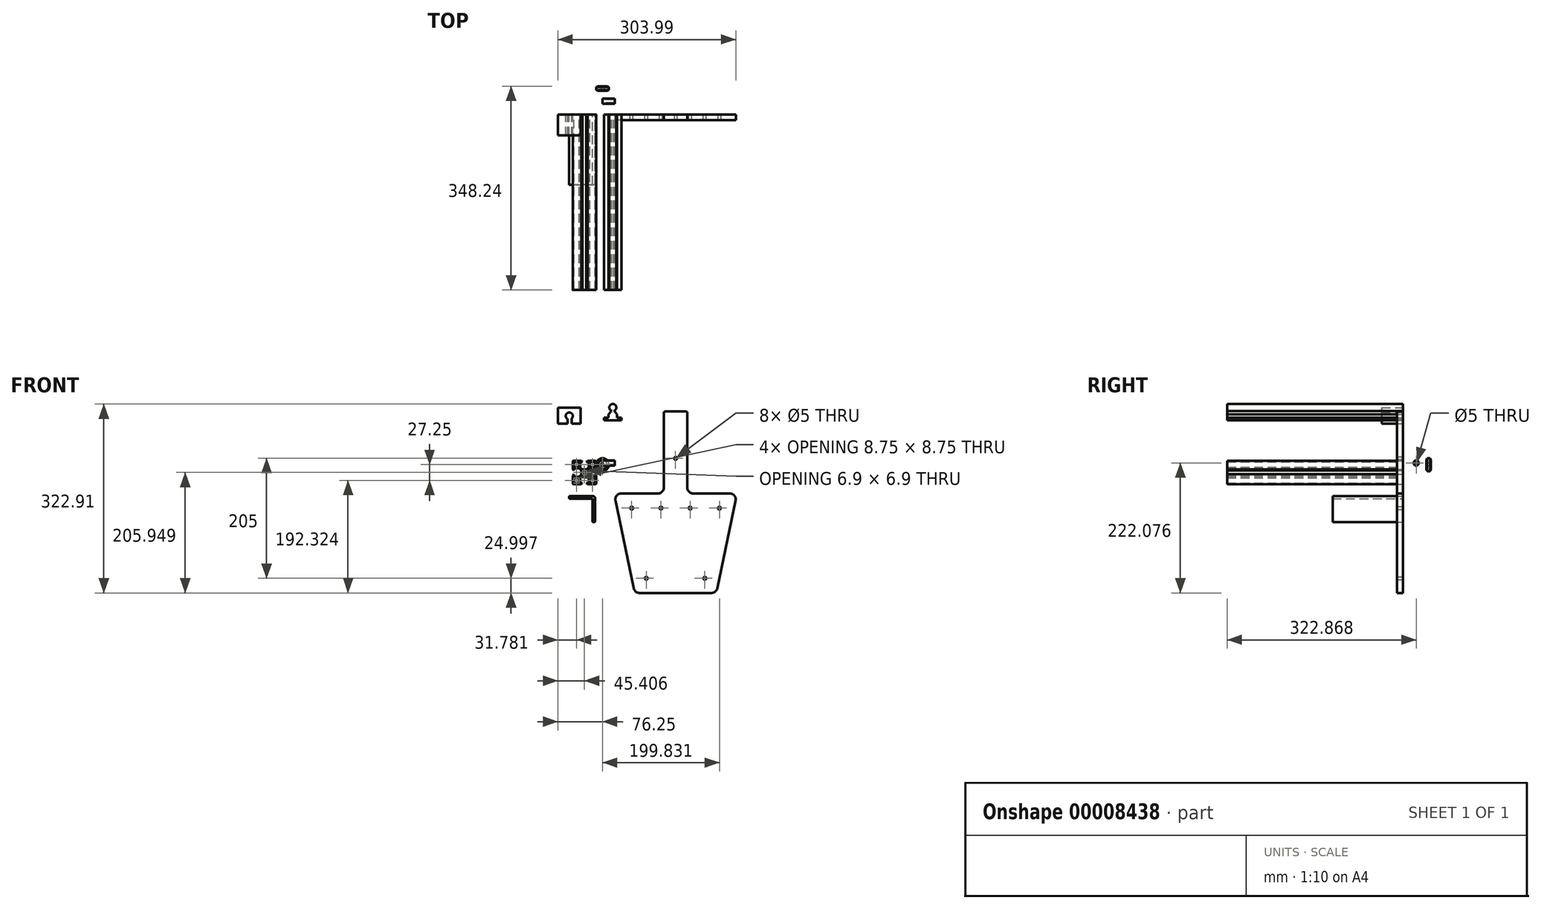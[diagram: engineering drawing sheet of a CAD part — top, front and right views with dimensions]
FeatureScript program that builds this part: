
annotation { "Feature Type Name" : "Feature", "Feature Type Description" : "" }
export const myFeature = defineFeature(function(context is Context, id is Id, definition is map)
    precondition{}
    {
        {
            var Q0;
            Q0=qCreatedBy(makeId("Front.planeOp"),FACE);
            var sketch = newSketch(context, id + "F0", { "sketchPlane" : qUnion([Q0])});
            skLineSegment(sketch, "E0", {"start": v(-49.84, 48.39) * mm, "end": v(-36.1, 48.39) * mm});
            skLineSegment(sketch, "E1", {"start": v(-36.1, 48.39) * mm, "end": v(-34.1, 46.39) * mm});
            skLineSegment(sketch, "E2", {"start": v(-34.1, 46.39) * mm, "end": v(-38.1, 46.39) * mm});
            skLineSegment(sketch, "E3", {"start": v(-48.84, 45.39) * mm, "end": v(-48.84, 38.64) * mm});
            skLineSegment(sketch, "E4", {"start": v(-48.84, 31.64) * mm, "end": v(-50.84, 33.64) * mm});
            skLineSegment(sketch, "E5", {"start": v(-50.84, 33.64) * mm, "end": v(-50.84, 47.39) * mm});
            skLineSegment(sketch, "E6", {"start": v(-50.84, 23.14) * mm, "end": v(-48.84, 25.14) * mm});
            skLineSegment(sketch, "E7", {"start": v(-48.84, 25.14) * mm, "end": v(-48.84, 22.14) * mm});
            skLineSegment(sketch, "E8", {"start": v(-47.84, 10.39) * mm, "end": v(-41.1, 10.39) * mm});
            skLineSegment(sketch, "E9", {"start": v(-34.1, 10.39) * mm, "end": v(-35.8, 8.68) * mm});
            skLineSegment(sketch, "E10", {"start": v(-36.5, 8.39) * mm, "end": v(-49.84, 8.39) * mm});
            skLineSegment(sketch, "E11", {"start": v(-50.84, 9.39) * mm, "end": v(-50.84, 23.14) * mm});
            skLineSegment(sketch, "E12", {"start": v(-25.6, 48.39) * mm, "end": v(-11.84, 48.39) * mm});
            skLineSegment(sketch, "E13", {"start": v(-10.84, 47.39) * mm, "end": v(-10.84, 33.64) * mm});
            skLineSegment(sketch, "E14", {"start": v(-10.84, 33.64) * mm, "end": v(-12.84, 31.64) * mm});
            skLineSegment(sketch, "E15", {"start": v(-12.84, 31.64) * mm, "end": v(-12.84, 34.64) * mm});
            skLineSegment(sketch, "E16", {"start": v(-13.84, 46.39) * mm, "end": v(-20.6, 46.39) * mm});
            skLineSegment(sketch, "E17", {"start": v(-27.6, 46.39) * mm, "end": v(-25.6, 48.39) * mm});
            skLineSegment(sketch, "E18", {"start": v(-10.84, 9.39) * mm, "end": v(-10.84, 22.72) * mm});
            skLineSegment(sketch, "E19", {"start": v(-11.14, 23.43) * mm, "end": v(-12.84, 25.14) * mm});
            skLineSegment(sketch, "E20", {"start": v(-12.84, 25.14) * mm, "end": v(-12.84, 22.14) * mm});
            skLineSegment(sketch, "E21", {"start": v(-13.84, 10.39) * mm, "end": v(-20.6, 10.39) * mm});
            skLineSegment(sketch, "E22", {"start": v(-27.6, 10.39) * mm, "end": v(-25.89, 8.68) * mm});
            skLineSegment(sketch, "E23", {"start": v(-25.18, 8.39) * mm, "end": v(-11.84, 8.39) * mm});
            skLineSegment(sketch, "E24", {"start": v(-48.84, 10.39) * mm, "end": v(-12.84, 46.39) * mm, "construction": true});
            skLineSegment(sketch, "E25", {"start": v(-48.84, 46.39) * mm, "end": v(-12.84, 10.39) * mm, "construction": true});
            skLineSegment(sketch, "E26", {"start": v(-40.1, 45.39) * mm, "end": v(-40.1, 38.64) * mm});
            skLineSegment(sketch, "E27", {"start": v(-41.1, 37.64) * mm, "end": v(-47.84, 37.64) * mm});
            skLineSegment(sketch, "E28", {"start": v(-13.84, 37.64) * mm, "end": v(-20.6, 37.64) * mm});
            skLineSegment(sketch, "E29", {"start": v(-21.6, 38.64) * mm, "end": v(-21.6, 45.39) * mm});
            skLineSegment(sketch, "E30", {"start": v(-47.84, 35.64) * mm, "end": v(-39.92, 35.64) * mm});
            skLineSegment(sketch, "E31", {"start": v(-38.1, 37.1) * mm, "end": v(-38.1, 46.39) * mm});
            skLineSegment(sketch, "E32", {"start": v(-23.6, 45.39) * mm, "end": v(-23.6, 37.47) * mm});
            skLineSegment(sketch, "E33", {"start": v(-21.77, 35.64) * mm, "end": v(-13.84, 35.64) * mm});
            skLineSegment(sketch, "E34.bottom", {"start": v(-34.74, 33.84) * mm, "end": v(-27.22, 33.84) * mm});
            skLineSegment(sketch, "E34.top", {"start": v(-34.46, 22.94) * mm, "end": v(-27.22, 22.94) * mm});
            skLineSegment(sketch, "E34.left", {"start": v(-36.3, 32) * mm, "end": v(-36.3, 24.77) * mm});
            skLineSegment(sketch, "E34.right", {"start": v(-25.4, 32) * mm, "end": v(-25.4, 24.77) * mm});
            skLineSegment(sketch, "E35.bottom", {"start": v(-33.3, 31.84) * mm, "end": v(-28.4, 31.84) * mm});
            skLineSegment(sketch, "E35.top", {"start": v(-33.3, 24.94) * mm, "end": v(-28.4, 24.94) * mm});
            skLineSegment(sketch, "E35.left", {"start": v(-34.3, 30.84) * mm, "end": v(-34.3, 25.94) * mm});
            skLineSegment(sketch, "E35.right", {"start": v(-27.4, 30.84) * mm, "end": v(-27.4, 25.94) * mm});
            skLineSegment(sketch, "E36", {"start": v(-23.89, 36.76) * mm, "end": v(-26.52, 34.13) * mm});
            skLineSegment(sketch, "E37", {"start": v(-25.1, 32.72) * mm, "end": v(-22.47, 35.35) * mm});
            skLineSegment(sketch, "E38", {"start": v(-35.44, 34.12) * mm, "end": v(-37.79, 36.39) * mm});
            skLineSegment(sketch, "E39", {"start": v(-47.84, 19.14) * mm, "end": v(-41.1, 19.14) * mm});
            skLineSegment(sketch, "E40", {"start": v(-40.1, 18.14) * mm, "end": v(-40.1, 11.39) * mm});
            skLineSegment(sketch, "E41", {"start": v(-47.84, 21.14) * mm, "end": v(-39.92, 21.14) * mm});
            skLineSegment(sketch, "E42", {"start": v(-38.1, 19.31) * mm, "end": v(-38.1, 11.39) * mm});
            skLineSegment(sketch, "E43", {"start": v(-21.6, 11.39) * mm, "end": v(-21.6, 18.14) * mm});
            skLineSegment(sketch, "E44", {"start": v(-20.6, 19.14) * mm, "end": v(-13.84, 19.14) * mm});
            skLineSegment(sketch, "E45", {"start": v(-21.77, 21.14) * mm, "end": v(-13.84, 21.14) * mm});
            skLineSegment(sketch, "E46", {"start": v(-23.6, 19.31) * mm, "end": v(-23.6, 11.39) * mm});
            skLineSegment(sketch, "E47", {"start": v(-35.17, 22.65) * mm, "end": v(-37.8, 20.02) * mm});
            skLineSegment(sketch, "E48", {"start": v(-39.22, 21.43) * mm, "end": v(-36.59, 24.06) * mm});
            skLineSegment(sketch, "E49", {"start": v(-22.47, 21.43) * mm, "end": v(-25.1, 24.06) * mm});
            skLineSegment(sketch, "E50", {"start": v(-36.59, 32.72) * mm, "end": v(-39.22, 35.35) * mm});
            skLineSegment(sketch, "E51", {"start": v(-23.89, 20.02) * mm, "end": v(-26.52, 22.65) * mm});
            skLineSegment(sketch, "E52.trimOffspring", {"start": v(-41.1, 46.39) * mm, "end": v(-47.84, 46.39) * mm});
            skLineSegment(sketch, "E53.trimOffspring", {"start": v(-48.84, 34.64) * mm, "end": v(-48.84, 31.64) * mm});
            skLineSegment(sketch, "E54.trimOffspring", {"start": v(-24.6, 46.39) * mm, "end": v(-27.6, 46.39) * mm});
            skLineSegment(sketch, "E55.trimOffspring", {"start": v(-12.84, 38.64) * mm, "end": v(-12.84, 45.39) * mm});
            skPoint(sketch, "E56.orphan", {"position": v(-23.6, 35.64) * mm});
            skLineSegment(sketch, "E57.trimOffspring", {"start": v(-12.84, 18.14) * mm, "end": v(-12.84, 11.39) * mm});
            skLineSegment(sketch, "E58.trimOffspring", {"start": v(-24.6, 10.39) * mm, "end": v(-27.6, 10.39) * mm});
            skLineSegment(sketch, "E59.trimOffspring", {"start": v(-37.1, 10.39) * mm, "end": v(-34.1, 10.39) * mm});
            skPoint(sketch, "E60.orphan", {"position": v(-38.1, 21.14) * mm});
            skLineSegment(sketch, "E61.trimOffspring", {"start": v(-48.84, 18.14) * mm, "end": v(-48.84, 11.39) * mm});
            skPoint(sketch, "E62.visualSharp", {"position": v(-48.84, 21.14) * mm});
            skArc(sketch, "E62.filletArc", {"start": v(-48.84, 22.14) * mm, "mid": v(-48.55, 21.43) * mm, "end": v(-47.84, 21.14) * mm});
            skPoint(sketch, "E63.visualSharp", {"position": v(-48.84, 19.14) * mm});
            skArc(sketch, "E63.filletArc", {"start": v(-47.84, 19.14) * mm, "mid": v(-48.55, 18.85) * mm, "end": v(-48.84, 18.14) * mm});
            skPoint(sketch, "E64.visualSharp", {"position": v(-40.1, 19.14) * mm});
            skArc(sketch, "E64.filletArc", {"start": v(-40.1, 18.14) * mm, "mid": v(-40.39, 18.85) * mm, "end": v(-41.1, 19.14) * mm});
            skPoint(sketch, "E65.visualSharp", {"position": v(-40.1, 10.39) * mm});
            skArc(sketch, "E65.filletArc", {"start": v(-41.1, 10.39) * mm, "mid": v(-40.39, 10.68) * mm, "end": v(-40.1, 11.39) * mm});
            skPoint(sketch, "E66.visualSharp", {"position": v(-48.84, 10.39) * mm});
            skArc(sketch, "E66.filletArc", {"start": v(-48.84, 11.39) * mm, "mid": v(-48.55, 10.68) * mm, "end": v(-47.84, 10.39) * mm});
            skPoint(sketch, "E67.visualSharp", {"position": v(-50.84, 8.39) * mm});
            skArc(sketch, "E67.filletArc", {"start": v(-50.84, 9.39) * mm, "mid": v(-50.55, 8.68) * mm, "end": v(-49.84, 8.39) * mm});
            skPoint(sketch, "E68.visualSharp", {"position": v(-36.1, 8.39) * mm});
            skArc(sketch, "E68.filletArc", {"start": v(-36.5, 8.39) * mm, "mid": v(-36.13, 8.46) * mm, "end": v(-35.8, 8.68) * mm});
            skPoint(sketch, "E69.visualSharp", {"position": v(-38.1, 10.39) * mm});
            skArc(sketch, "E69.filletArc", {"start": v(-38.1, 11.39) * mm, "mid": v(-37.8, 10.68) * mm, "end": v(-37.1, 10.39) * mm});
            skPoint(sketch, "E70.visualSharp", {"position": v(-38.1, 19.72) * mm});
            skArc(sketch, "E70.filletArc", {"start": v(-37.8, 20.02) * mm, "mid": v(-38.02, 19.7) * mm, "end": v(-38.1, 19.31) * mm});
            skPoint(sketch, "E71.visualSharp", {"position": v(-39.5, 21.14) * mm});
            skArc(sketch, "E71.filletArc", {"start": v(-39.92, 21.14) * mm, "mid": v(-39.54, 21.21) * mm, "end": v(-39.22, 21.43) * mm});
            skPoint(sketch, "E72.visualSharp", {"position": v(-34.88, 22.94) * mm});
            skArc(sketch, "E72.filletArc", {"start": v(-34.46, 22.94) * mm, "mid": v(-34.85, 22.86) * mm, "end": v(-35.17, 22.65) * mm});
            skPoint(sketch, "E73.visualSharp", {"position": v(-36.3, 24.35) * mm});
            skArc(sketch, "E73.filletArc", {"start": v(-36.59, 24.06) * mm, "mid": v(-36.37, 24.39) * mm, "end": v(-36.3, 24.77) * mm});
            skPoint(sketch, "E74.visualSharp", {"position": v(-10.84, 8.39) * mm});
            skArc(sketch, "E74.filletArc", {"start": v(-11.84, 8.39) * mm, "mid": v(-11.14, 8.68) * mm, "end": v(-10.84, 9.39) * mm});
            skPoint(sketch, "E75.visualSharp", {"position": v(-12.84, 10.39) * mm});
            skArc(sketch, "E75.filletArc", {"start": v(-13.84, 10.39) * mm, "mid": v(-13.14, 10.68) * mm, "end": v(-12.84, 11.39) * mm});
            skPoint(sketch, "E76.visualSharp", {"position": v(-21.6, 10.39) * mm});
            skArc(sketch, "E76.filletArc", {"start": v(-21.6, 11.39) * mm, "mid": v(-21.3, 10.68) * mm, "end": v(-20.6, 10.39) * mm});
            skPoint(sketch, "E77.visualSharp", {"position": v(-23.6, 10.39) * mm});
            skArc(sketch, "E77.filletArc", {"start": v(-24.6, 10.39) * mm, "mid": v(-23.89, 10.68) * mm, "end": v(-23.6, 11.39) * mm});
            skPoint(sketch, "E78.visualSharp", {"position": v(-25.6, 8.39) * mm});
            skArc(sketch, "E78.filletArc", {"start": v(-25.89, 8.68) * mm, "mid": v(-25.56, 8.46) * mm, "end": v(-25.18, 8.39) * mm});
            skPoint(sketch, "E79.visualSharp", {"position": v(-12.84, 19.14) * mm});
            skArc(sketch, "E79.filletArc", {"start": v(-12.84, 18.14) * mm, "mid": v(-13.14, 18.85) * mm, "end": v(-13.84, 19.14) * mm});
            skPoint(sketch, "E80.visualSharp", {"position": v(-21.6, 19.14) * mm});
            skArc(sketch, "E80.filletArc", {"start": v(-20.6, 19.14) * mm, "mid": v(-21.3, 18.85) * mm, "end": v(-21.6, 18.14) * mm});
            skPoint(sketch, "E81.orphan", {"position": v(-23.6, 21.14) * mm});
            skPoint(sketch, "E82.visualSharp", {"position": v(-12.84, 21.14) * mm});
            skArc(sketch, "E82.filletArc", {"start": v(-13.84, 21.14) * mm, "mid": v(-13.14, 21.43) * mm, "end": v(-12.84, 22.14) * mm});
            skPoint(sketch, "E83.visualSharp", {"position": v(-10.84, 23.14) * mm});
            skArc(sketch, "E83.filletArc", {"start": v(-10.84, 22.72) * mm, "mid": v(-10.92, 23.1) * mm, "end": v(-11.14, 23.43) * mm});
            skPoint(sketch, "E84.visualSharp", {"position": v(-23.6, 19.72) * mm});
            skArc(sketch, "E84.filletArc", {"start": v(-23.6, 19.31) * mm, "mid": v(-23.67, 19.7) * mm, "end": v(-23.89, 20.02) * mm});
            skPoint(sketch, "E85.visualSharp", {"position": v(-26.81, 22.94) * mm});
            skArc(sketch, "E85.filletArc", {"start": v(-26.52, 22.65) * mm, "mid": v(-26.84, 22.86) * mm, "end": v(-27.22, 22.94) * mm});
            skPoint(sketch, "E86.visualSharp", {"position": v(-22.18, 21.14) * mm});
            skArc(sketch, "E86.filletArc", {"start": v(-22.47, 21.43) * mm, "mid": v(-22.15, 21.21) * mm, "end": v(-21.77, 21.14) * mm});
            skPoint(sketch, "E87.visualSharp", {"position": v(-25.4, 24.35) * mm});
            skArc(sketch, "E87.filletArc", {"start": v(-25.4, 24.77) * mm, "mid": v(-25.32, 24.39) * mm, "end": v(-25.1, 24.06) * mm});
            skPoint(sketch, "E88.visualSharp", {"position": v(-27.4, 24.94) * mm});
            skArc(sketch, "E88.filletArc", {"start": v(-28.4, 24.94) * mm, "mid": v(-27.69, 25.23) * mm, "end": v(-27.4, 25.94) * mm});
            skPoint(sketch, "E89.visualSharp", {"position": v(-34.3, 24.94) * mm});
            skArc(sketch, "E89.filletArc", {"start": v(-34.3, 25.94) * mm, "mid": v(-34, 25.23) * mm, "end": v(-33.3, 24.94) * mm});
            skPoint(sketch, "E90.visualSharp", {"position": v(-34.3, 31.84) * mm});
            skArc(sketch, "E90.filletArc", {"start": v(-33.3, 31.84) * mm, "mid": v(-34, 31.54) * mm, "end": v(-34.3, 30.84) * mm});
            skPoint(sketch, "E91.visualSharp", {"position": v(-27.4, 31.84) * mm});
            skArc(sketch, "E91.filletArc", {"start": v(-27.4, 30.84) * mm, "mid": v(-27.69, 31.54) * mm, "end": v(-28.4, 31.84) * mm});
            skPoint(sketch, "E92.visualSharp", {"position": v(-25.4, 32.42) * mm});
            skArc(sketch, "E92.filletArc", {"start": v(-25.1, 32.72) * mm, "mid": v(-25.32, 32.4) * mm, "end": v(-25.4, 32) * mm});
            skPoint(sketch, "E93.visualSharp", {"position": v(-22.18, 35.64) * mm});
            skArc(sketch, "E93.filletArc", {"start": v(-21.77, 35.64) * mm, "mid": v(-22.15, 35.56) * mm, "end": v(-22.47, 35.35) * mm});
            skPoint(sketch, "E94.visualSharp", {"position": v(-12.84, 35.64) * mm});
            skArc(sketch, "E94.filletArc", {"start": v(-12.84, 34.64) * mm, "mid": v(-13.14, 35.35) * mm, "end": v(-13.84, 35.64) * mm});
            skPoint(sketch, "E95.visualSharp", {"position": v(-12.84, 37.64) * mm});
            skArc(sketch, "E95.filletArc", {"start": v(-13.84, 37.64) * mm, "mid": v(-13.14, 37.93) * mm, "end": v(-12.84, 38.64) * mm});
            skPoint(sketch, "E96.visualSharp", {"position": v(-21.6, 37.64) * mm});
            skArc(sketch, "E96.filletArc", {"start": v(-21.6, 38.64) * mm, "mid": v(-21.3, 37.93) * mm, "end": v(-20.6, 37.64) * mm});
            skPoint(sketch, "E97.visualSharp", {"position": v(-23.6, 37.05) * mm});
            skArc(sketch, "E97.filletArc", {"start": v(-23.89, 36.76) * mm, "mid": v(-23.67, 37.08) * mm, "end": v(-23.6, 37.47) * mm});
            skPoint(sketch, "E98.visualSharp", {"position": v(-26.81, 33.84) * mm});
            skArc(sketch, "E98.filletArc", {"start": v(-27.22, 33.84) * mm, "mid": v(-26.84, 33.91) * mm, "end": v(-26.52, 34.13) * mm});
            skPoint(sketch, "E99.visualSharp", {"position": v(-35.15, 33.84) * mm});
            skArc(sketch, "E99.filletArc", {"start": v(-35.44, 34.12) * mm, "mid": v(-35.12, 33.91) * mm, "end": v(-34.74, 33.84) * mm});
            skPoint(sketch, "E100.visualSharp", {"position": v(-38.1, 36.68) * mm});
            skArc(sketch, "E100.filletArc", {"start": v(-38.1, 37.1) * mm, "mid": v(-38.01, 36.72) * mm, "end": v(-37.79, 36.39) * mm});
            skPoint(sketch, "E101.visualSharp", {"position": v(-36.3, 32.42) * mm});
            skArc(sketch, "E101.filletArc", {"start": v(-36.3, 32) * mm, "mid": v(-36.37, 32.4) * mm, "end": v(-36.59, 32.72) * mm});
            skPoint(sketch, "E102.visualSharp", {"position": v(-39.5, 35.64) * mm});
            skArc(sketch, "E102.filletArc", {"start": v(-39.22, 35.35) * mm, "mid": v(-39.54, 35.56) * mm, "end": v(-39.92, 35.64) * mm});
            skPoint(sketch, "E103.visualSharp", {"position": v(-12.84, 46.39) * mm});
            skArc(sketch, "E103.filletArc", {"start": v(-12.84, 45.39) * mm, "mid": v(-13.14, 46.1) * mm, "end": v(-13.84, 46.39) * mm});
            skPoint(sketch, "E104.visualSharp", {"position": v(-10.84, 48.39) * mm});
            skArc(sketch, "E104.filletArc", {"start": v(-10.84, 47.39) * mm, "mid": v(-11.14, 48.1) * mm, "end": v(-11.84, 48.39) * mm});
            skPoint(sketch, "E105.visualSharp", {"position": v(-23.6, 46.39) * mm});
            skArc(sketch, "E105.filletArc", {"start": v(-23.6, 45.39) * mm, "mid": v(-23.89, 46.1) * mm, "end": v(-24.6, 46.39) * mm});
            skPoint(sketch, "E106.visualSharp", {"position": v(-21.6, 46.39) * mm});
            skArc(sketch, "E106.filletArc", {"start": v(-20.6, 46.39) * mm, "mid": v(-21.3, 46.1) * mm, "end": v(-21.6, 45.39) * mm});
            skPoint(sketch, "E107.visualSharp", {"position": v(-48.84, 35.64) * mm});
            skArc(sketch, "E107.filletArc", {"start": v(-47.84, 35.64) * mm, "mid": v(-48.55, 35.35) * mm, "end": v(-48.84, 34.64) * mm});
            skPoint(sketch, "E108.visualSharp", {"position": v(-48.84, 37.64) * mm});
            skArc(sketch, "E108.filletArc", {"start": v(-48.84, 38.64) * mm, "mid": v(-48.55, 37.93) * mm, "end": v(-47.84, 37.64) * mm});
            skPoint(sketch, "E109.visualSharp", {"position": v(-50.84, 48.39) * mm});
            skArc(sketch, "E109.filletArc", {"start": v(-49.84, 48.39) * mm, "mid": v(-50.55, 48.1) * mm, "end": v(-50.84, 47.39) * mm});
            skPoint(sketch, "E110.visualSharp", {"position": v(-48.84, 46.39) * mm});
            skArc(sketch, "E110.filletArc", {"start": v(-47.84, 46.39) * mm, "mid": v(-48.55, 46.1) * mm, "end": v(-48.84, 45.39) * mm});
            skPoint(sketch, "E111.visualSharp", {"position": v(-40.1, 46.39) * mm});
            skArc(sketch, "E111.filletArc", {"start": v(-40.1, 45.39) * mm, "mid": v(-40.39, 46.1) * mm, "end": v(-41.1, 46.39) * mm});
            skPoint(sketch, "E112.visualSharp", {"position": v(-40.1, 37.64) * mm});
            skArc(sketch, "E112.filletArc", {"start": v(-41.1, 37.64) * mm, "mid": v(-40.39, 37.93) * mm, "end": v(-40.1, 38.64) * mm});
            skSolve(sketch);
        }
        {
            var Q0;
            Q0=makeQuery(id+"F0.imprint","IMPRINT",FACE,{"disambiguationData":[TD([[makeQuery(id+"F0.imprint","IMPRINT",EDGE,{"derivedFrom":sQuery(id+"F0.wireOp",EDGE,"E0")}),-1.0]])]});
            extrude(context, id + "F1", {"entities" : qUnion([Q0]), "depth" : 300 * mm});
        }
        {
            var Q0;
            Q0=qCreatedBy(makeId("Front.planeOp"),FACE);
            var sketch = newSketch(context, id + "F2", { "sketchPlane" : qUnion([Q0])});
            skLineSegment(sketch, "E113", {"start": v(-55.84, -12.26) * mm, "end": v(-15.84, -12.26) * mm});
            skLineSegment(sketch, "E114", {"start": v(-12.84, -15.26) * mm, "end": v(-12.84, -55.26) * mm});
            skLineSegment(sketch, "E115", {"start": v(-13.84, -56.26) * mm, "end": v(-15.84, -56.26) * mm});
            skLineSegment(sketch, "E116", {"start": v(-16.84, -55.26) * mm, "end": v(-16.84, -17.26) * mm});
            skLineSegment(sketch, "E117", {"start": v(-17.84, -16.26) * mm, "end": v(-55.84, -16.26) * mm});
            skLineSegment(sketch, "E118", {"start": v(-56.84, -15.26) * mm, "end": v(-56.84, -13.26) * mm});
            skPoint(sketch, "E119.visualSharp", {"position": v(-56.84, -12.26) * mm});
            skArc(sketch, "E119.filletArc", {"start": v(-55.84, -12.26) * mm, "mid": v(-56.55, -12.56) * mm, "end": v(-56.84, -13.26) * mm});
            skPoint(sketch, "E120.visualSharp", {"position": v(-56.84, -16.26) * mm});
            skArc(sketch, "E120.filletArc", {"start": v(-56.84, -15.26) * mm, "mid": v(-56.55, -15.97) * mm, "end": v(-55.84, -16.26) * mm});
            skPoint(sketch, "E121.visualSharp", {"position": v(-16.84, -16.26) * mm});
            skArc(sketch, "E121.filletArc", {"start": v(-16.84, -17.26) * mm, "mid": v(-17.13, -16.56) * mm, "end": v(-17.84, -16.26) * mm});
            skPoint(sketch, "E122.visualSharp", {"position": v(-12.84, -56.26) * mm});
            skArc(sketch, "E122.filletArc", {"start": v(-13.84, -56.26) * mm, "mid": v(-13.13, -55.97) * mm, "end": v(-12.84, -55.26) * mm});
            skPoint(sketch, "E123.visualSharp", {"position": v(-16.84, -56.26) * mm});
            skArc(sketch, "E123.filletArc", {"start": v(-16.84, -55.26) * mm, "mid": v(-16.55, -55.97) * mm, "end": v(-15.84, -56.26) * mm});
            skPoint(sketch, "E124.visualSharp", {"position": v(-12.84, -12.26) * mm});
            skArc(sketch, "E124.filletArc", {"start": v(-12.84, -15.26) * mm, "mid": v(-13.72, -13.14) * mm, "end": v(-15.84, -12.26) * mm});
            skSolve(sketch);
        }
        {
            var Q0;
            Q0=makeQuery(id+"F2.imprint","IMPRINT",FACE,{"disambiguationData":[TD([[makeQuery(id+"F2.imprint","IMPRINT",EDGE,{"derivedFrom":sQuery(id+"F2.wireOp",EDGE,"E113")}),-1.0]])]});
            extrude(context, id + "F3", {"entities" : qUnion([Q0]), "depth" : 120 * mm});
        }
        {
            var Q0;
            Q0=qCreatedBy(makeId("Front.planeOp"),FACE);
            var sketch = newSketch(context, id + "F4", { "sketchPlane" : qUnion([Q0])});
            skLineSegment(sketch, "E125", {"start": v(-8.08, -7.56) * mm, "end": v(54.83, -7.56) * mm});
            skLineSegment(sketch, "E126", {"start": v(187.53, -19.6) * mm, "end": v(156.28, -169.6) * mm});
            skLineSegment(sketch, "E127", {"start": v(146.5, -177.56) * mm, "end": v(23.17, -177.56) * mm});
            skLineSegment(sketch, "E128", {"start": v(13.38, -169.6) * mm, "end": v(-17.87, -19.6) * mm});
            skPoint(sketch, "E129", {"position": v(84.83, -7.56) * mm});
            skPoint(sketch, "E130", {"position": v(84.83, -177.56) * mm});
            skLineSegment(sketch, "E131", {"start": v(84.83, -177.56) * mm, "end": v(84.83, -7.56) * mm, "construction": true});
            skPoint(sketch, "E132.visualSharp", {"position": v(190.04, -7.56) * mm});
            skArc(sketch, "E132.filletArc", {"start": v(187.53, -19.6) * mm, "mid": v(185.5, -11.25) * mm, "end": v(177.74, -7.56) * mm});
            skPoint(sketch, "E133.visualSharp", {"position": v(-20.38, -7.56) * mm});
            skArc(sketch, "E133.filletArc", {"start": v(-8.08, -7.56) * mm, "mid": v(-15.84, -11.25) * mm, "end": v(-17.87, -19.6) * mm});
            skPoint(sketch, "E134.visualSharp", {"position": v(15.04, -177.56) * mm});
            skArc(sketch, "E134.filletArc", {"start": v(13.38, -169.6) * mm, "mid": v(16.86, -175.32) * mm, "end": v(23.17, -177.56) * mm});
            skPoint(sketch, "E135.visualSharp", {"position": v(154.62, -177.56) * mm});
            skArc(sketch, "E135.filletArc", {"start": v(146.5, -177.56) * mm, "mid": v(152.8, -175.32) * mm, "end": v(156.28, -169.6) * mm});
            skLineSegment(sketch, "E136", {"start": v(9.83, -152.56) * mm, "end": v(159.83, -152.56) * mm, "construction": true});
            skLineSegment(sketch, "E137", {"start": v(-15.17, -32.56) * mm, "end": v(184.83, -32.56) * mm, "construction": true});
            skCircle(sketch, "E138", {"center": v(9.83, -32.56) * mm, "radius": 2.5 * mm});
            skCircle(sketch, "E139", {"center": v(59.83, -32.56) * mm, "radius": 2.5 * mm});
            skCircle(sketch, "E140", {"center": v(109.83, -32.56) * mm, "radius": 2.5 * mm});
            skCircle(sketch, "E141", {"center": v(159.83, -32.56) * mm, "radius": 2.5 * mm});
            skCircle(sketch, "E142", {"center": v(34.83, -152.56) * mm, "radius": 2.5 * mm});
            skCircle(sketch, "E143", {"center": v(134.83, -152.56) * mm, "radius": 2.5 * mm});
            skLineSegment(sketch, "E144", {"start": v(34.83, -141.56) * mm, "end": v(134.83, -141.56) * mm, "construction": true});
            skLineSegment(sketch, "E145", {"start": v(9.83, -59.91) * mm, "end": v(59.83, -59.91) * mm, "construction": true});
            skLineSegment(sketch, "E146", {"start": v(59.83, -59.91) * mm, "end": v(109.83, -59.91) * mm, "construction": true});
            skLineSegment(sketch, "E147", {"start": v(109.83, -59.91) * mm, "end": v(159.83, -59.91) * mm, "construction": true});
            skPoint(sketch, "E148", {"position": v(84.83, -59.91) * mm});
            skPoint(sketch, "E149", {"position": v(84.83, -141.56) * mm});
            skPoint(sketch, "E150", {"position": v(34.83, -59.91) * mm});
            skPoint(sketch, "E151", {"position": v(134.83, -59.91) * mm});
            skLineSegment(sketch, "E152", {"start": v(64.83, 2.44) * mm, "end": v(64.83, 130.44) * mm});
            skLineSegment(sketch, "E153", {"start": v(66.83, 132.44) * mm, "end": v(102.83, 132.44) * mm});
            skLineSegment(sketch, "E154", {"start": v(104.83, 130.44) * mm, "end": v(104.83, 2.44) * mm});
            skLineSegment(sketch, "E155.trimOffspring", {"start": v(114.83, -7.56) * mm, "end": v(177.74, -7.56) * mm});
            skPoint(sketch, "E156", {"position": v(84.83, 132.44) * mm});
            skPoint(sketch, "E157.visualSharp", {"position": v(104.83, -7.56) * mm});
            skArc(sketch, "E157.filletArc", {"start": v(104.83, 2.44) * mm, "mid": v(107.76, -4.63) * mm, "end": v(114.83, -7.56) * mm});
            skPoint(sketch, "E158.visualSharp", {"position": v(64.83, -7.56) * mm});
            skArc(sketch, "E158.filletArc", {"start": v(54.83, -7.56) * mm, "mid": v(61.9, -4.63) * mm, "end": v(64.83, 2.44) * mm});
            skPoint(sketch, "E159.visualSharp", {"position": v(104.83, 132.44) * mm});
            skArc(sketch, "E159.filletArc", {"start": v(104.83, 130.44) * mm, "mid": v(104.25, 131.85) * mm, "end": v(102.83, 132.44) * mm});
            skPoint(sketch, "E160.visualSharp", {"position": v(64.83, 132.44) * mm});
            skArc(sketch, "E160.filletArc", {"start": v(66.83, 132.44) * mm, "mid": v(65.42, 131.85) * mm, "end": v(64.83, 130.44) * mm});
            skSolve(sketch);
        }
        {
            var Q0;
            Q0=makeQuery(id+"F4.imprint","IMPRINT",FACE,{"disambiguationData":[TD([[makeQuery(id+"F4.imprint","IMPRINT",EDGE,{"derivedFrom":sQuery(id+"F4.wireOp",EDGE,"E125")}),-1.0]])]});
            extrude(context, id + "F5", {"entities" : qUnion([Q0]), "depth" : 10 * mm});
        }
        {
            var Q0;
            Q0=makeQuery(id+"F5.opExtrude","SWEPT_BODY",BODY,{"disambiguationData":[OSD([sQuery(id+"F4.wireOp",EDGE,"E125"),sQuery(id+"F4.wireOp",EDGE,"E126"),sQuery(id+"F4.wireOp",EDGE,"E127"),sQuery(id+"F4.wireOp",EDGE,"E128"),sQuery(id+"F4.wireOp",EDGE,"E132.filletArc"),sQuery(id+"F4.wireOp",EDGE,"E133.filletArc"),sQuery(id+"F4.wireOp",EDGE,"E134.filletArc"),sQuery(id+"F4.wireOp",EDGE,"E135.filletArc"),sQuery(id+"F4.wireOp",EDGE,"E138"),sQuery(id+"F4.wireOp",EDGE,"E139"),sQuery(id+"F4.wireOp",EDGE,"E140"),sQuery(id+"F4.wireOp",EDGE,"E141"),sQuery(id+"F4.wireOp",EDGE,"E142"),sQuery(id+"F4.wireOp",EDGE,"E143"),sQuery(id+"F4.wireOp",EDGE,"E152"),sQuery(id+"F4.wireOp",EDGE,"E153"),sQuery(id+"F4.wireOp",EDGE,"E154"),sQuery(id+"F4.wireOp",EDGE,"E155.trimOffspring"),sQuery(id+"F4.wireOp",EDGE,"E157.filletArc"),sQuery(id+"F4.wireOp",EDGE,"E158.filletArc"),sQuery(id+"F4.wireOp",EDGE,"E159.filletArc"),sQuery(id+"F4.wireOp",EDGE,"E160.filletArc")])]});
            transform(context, id + "F6", {"entities" : qUnion([Q0]), "transformType" : TransformType.TRANSLATION_3D, "dx" : 40 * mm, "dy" : 0 * mm, "dz" : 0 * mm, "makeCopy" : false});
        }
        {
            var Q0;
            Q0=qCreatedBy(makeId("Right.planeOp"),FACE);
            var sketch = newSketch(context, id + "F7", { "sketchPlane" : qUnion([Q0])});
            skLineSegment(sketch, "E161", {"start": v(41.74, 52.7) * mm, "end": v(46.74, 52.7) * mm});
            skLineSegment(sketch, "E162", {"start": v(46.74, 52.7) * mm, "end": v(48.24, 49.13) * mm});
            skLineSegment(sketch, "E163", {"start": v(48.24, 49.13) * mm, "end": v(48.24, 44.2) * mm});
            skLineSegment(sketch, "E164", {"start": v(41.74, 52.7) * mm, "end": v(40.24, 49.13) * mm});
            skLineSegment(sketch, "E165", {"start": v(40.24, 49.13) * mm, "end": v(40.24, 44.2) * mm});
            skLineSegment(sketch, "E166", {"start": v(40.24, 44.2) * mm, "end": v(48.24, 44.2) * mm});
            skPoint(sketch, "E167", {"position": v(44.24, 44.2) * mm});
            skPoint(sketch, "E168", {"position": v(44.24, 52.7) * mm});
            skLineSegment(sketch, "E169", {"start": v(40.24, 41.7) * mm, "end": v(48.24, 41.7) * mm, "construction": true});
            skSolve(sketch);
        }
        {
            var Q0;
            Q0=makeQuery(id+"F7.imprint","IMPRINT",FACE,{"disambiguationData":[TD([[makeQuery(id+"F7.imprint","IMPRINT",EDGE,{"derivedFrom":sQuery(id+"F7.wireOp",EDGE,"E161")}),-1.0]])]});
            var Q1;
            Q1=sQuery(id+"F7.wireOp",EDGE,"E169");
            revolve(context, id + "F8", {"entities" : qUnion([Q0]), "axis" : qUnion([Q1]), "revolveType" : RevolveType.FULL});
        }
        {
            var Q0;
            Q0=qCreatedBy(makeId("Right.planeOp"),FACE);
            var sketch = newSketch(context, id + "F9", { "sketchPlane" : qUnion([Q0])});
            skLineSegment(sketch, "E170.0", {"start": v(40.24, 34.26) * mm, "end": v(40.24, 49.13) * mm, "construction": true});
            skPoint(sketch, "E171", {"position": v(40.24, 60.88) * mm});
            skLineSegment(sketch, "E172", {"start": v(40.24, 60.88) * mm, "end": v(19.24, 60.88) * mm, "construction": true});
            skLineSegment(sketch, "E173", {"start": v(44.24, 65.5) * mm, "end": v(19.24, 65.5) * mm, "construction": true});
            skPoint(sketch, "E174", {"position": v(46.74, 52.7) * mm});
            skLineSegment(sketch, "E175", {"start": v(41.74, 52.7) * mm, "end": v(46.74, 52.7) * mm, "construction": true});
            skPoint(sketch, "E176", {"position": v(44.24, 52.7) * mm});
            skCircle(sketch, "E177", {"center": v(22.87, 44.52) * mm, "radius": 2.5 * mm});
            skCircle(sketch, "E178", {"center": v(22.87, 44.52) * mm, "radius": 4.5 * mm});
            skSolve(sketch);
        }
        {
            var Q0;
            Q0=makeQuery(id+"F9.imprint","IMPRINT",FACE,{"disambiguationData":[TD([[makeQuery(id+"F9.imprint","IMPRINT",EDGE,{"derivedFrom":sQuery(id+"F9.wireOp",EDGE,"E177")}),-1.0]])]});
            extrude(context, id + "F10", {"entities" : qUnion([Q0]), "depth" : 21 * mm});
        }
        {
            var Q0;
            Q0=makeQuery(id+"F5.opExtrude","CAP_FACE",FACE,{"disambiguationData":[OSD([sQuery(id+"F4.wireOp",EDGE,"E125"),sQuery(id+"F4.wireOp",EDGE,"E126"),sQuery(id+"F4.wireOp",EDGE,"E127"),sQuery(id+"F4.wireOp",EDGE,"E128"),sQuery(id+"F4.wireOp",EDGE,"E132.filletArc"),sQuery(id+"F4.wireOp",EDGE,"E133.filletArc"),sQuery(id+"F4.wireOp",EDGE,"E134.filletArc"),sQuery(id+"F4.wireOp",EDGE,"E135.filletArc"),sQuery(id+"F4.wireOp",EDGE,"E138"),sQuery(id+"F4.wireOp",EDGE,"E139"),sQuery(id+"F4.wireOp",EDGE,"E140"),sQuery(id+"F4.wireOp",EDGE,"E141"),sQuery(id+"F4.wireOp",EDGE,"E142"),sQuery(id+"F4.wireOp",EDGE,"E143"),sQuery(id+"F4.wireOp",EDGE,"E152"),sQuery(id+"F4.wireOp",EDGE,"E153"),sQuery(id+"F4.wireOp",EDGE,"E154"),sQuery(id+"F4.wireOp",EDGE,"E155.trimOffspring"),sQuery(id+"F4.wireOp",EDGE,"E157.filletArc"),sQuery(id+"F4.wireOp",EDGE,"E158.filletArc"),sQuery(id+"F4.wireOp",EDGE,"E159.filletArc"),sQuery(id+"F4.wireOp",EDGE,"E160.filletArc")])],"isStart":false});
            var sketch = newSketch(context, id + "F11", { "sketchPlane" : qUnion([Q0])});
            skPoint(sketch, "E179", {"position": v(124.83, 132.44) * mm});
            skLineSegment(sketch, "E180", {"start": v(124.83, 132.44) * mm, "end": v(124.83, 52.44) * mm, "construction": true});
            skCircle(sketch, "E181", {"center": v(124.83, 52.44) * mm, "radius": 2.5 * mm});
            skSolve(sketch);
        }
        {
            var Q0;
            Q0=makeQuery(id+"F11.imprint","IMPRINT",FACE,{"disambiguationData":[TD([[makeQuery(id+"F11.imprint","IMPRINT",EDGE,{"derivedFrom":sQuery(id+"F11.wireOp",EDGE,"E181")}),1.0]])]});
            extrude(context, id + "F12", {"entities" : qUnion([Q0]), "operationType" : NewBodyOperationType.REMOVE, "endBound" : BoundingType.UP_TO_NEXT, "oppositeDirection" : true, "depth" : 25 * mm});
        }
        {
            var Q0;
            Q0=qCreatedBy(makeId("Front.planeOp"),FACE);
            var sketch = newSketch(context, id + "F13", { "sketchPlane" : qUnion([Q0])});
            skCircle(sketch, "E182", {"center": v(17.64, 139.35) * mm, "radius": 6 * mm});
            skLineSegment(sketch, "E183.bottom", {"start": v(2.64, 122) * mm, "end": v(32.64, 122) * mm});
            skLineSegment(sketch, "E183.top", {"start": v(2.64, 117.35) * mm, "end": v(32.64, 117.35) * mm});
            skLineSegment(sketch, "E183.left", {"start": v(2.64, 122) * mm, "end": v(2.64, 117.35) * mm});
            skLineSegment(sketch, "E183.right", {"start": v(32.64, 122) * mm, "end": v(32.64, 117.35) * mm});
            skLineSegment(sketch, "E184.bottom", {"start": v(25.14, 127.53) * mm, "end": v(10.14, 127.53) * mm});
            skLineSegment(sketch, "E184.top", {"start": v(25.14, 122) * mm, "end": v(10.14, 122) * mm});
            skLineSegment(sketch, "E184.left", {"start": v(25.14, 127.53) * mm, "end": v(25.14, 122) * mm});
            skLineSegment(sketch, "E184.right", {"start": v(10.14, 127.53) * mm, "end": v(10.14, 122) * mm});
            skLineSegment(sketch, "E185", {"start": v(10.14, 127.53) * mm, "end": v(15.14, 133.5) * mm});
            skLineSegment(sketch, "E186", {"start": v(15.14, 133.5) * mm, "end": v(20.13, 133.52) * mm});
            skLineSegment(sketch, "E187", {"start": v(20.13, 133.52) * mm, "end": v(25.14, 127.53) * mm});
            skPoint(sketch, "E188", {"position": v(17.64, 127.53) * mm});
            skPoint(sketch, "E189", {"position": v(17.64, 133.52) * mm});
            skPoint(sketch, "E190", {"position": v(17.64, 122) * mm});
            skPoint(sketch, "E191", {"position": v(17.64, 145.35) * mm});
            skSolve(sketch);
        }
        {
            var Q0;
            Q0=qCreatedBy(makeId("Front.planeOp"),FACE);
            var sketch = newSketch(context, id + "F14", { "sketchPlane" : qUnion([Q0])});
            skArc(sketch, "E192", {"start": v(-52.9, 120.27) * mm, "mid": v(-57.2, 130.84) * mm, "end": v(-59.9, 119.74) * mm});
            skLineSegment(sketch, "E193", {"start": v(-59.9, 119.74) * mm, "end": v(-59.9, 112.05) * mm});
            skLineSegment(sketch, "E194", {"start": v(-59.9, 112.05) * mm, "end": v(-76.25, 112.05) * mm});
            skLineSegment(sketch, "E195", {"start": v(-76.25, 112.05) * mm, "end": v(-76.25, 139.05) * mm});
            skLineSegment(sketch, "E196", {"start": v(-76.25, 139.05) * mm, "end": v(-37.25, 139.05) * mm});
            skLineSegment(sketch, "E197", {"start": v(-37.25, 139.05) * mm, "end": v(-37.25, 112.05) * mm});
            skLineSegment(sketch, "E198", {"start": v(-37.25, 112.05) * mm, "end": v(-52.9, 112.05) * mm});
            skLineSegment(sketch, "E199", {"start": v(-52.9, 112.05) * mm, "end": v(-52.9, 120.27) * mm});
            skPoint(sketch, "E200", {"position": v(-56.75, 139.05) * mm});
            skPoint(sketch, "E201", {"position": v(-56.75, 130.84) * mm});
            skPoint(sketch, "E201.positionSnap0", {"position": v(-57.2, 130.84) * mm});
            skLineSegment(sketch, "E202", {"start": v(-57.2, 130.84) * mm, "end": v(-56.75, 139.05) * mm, "construction": true});
            skSolve(sketch);
        }
        {
            var Q0;
            Q0=makeQuery(id+"F14.imprint","IMPRINT",FACE,{"disambiguationData":[TD([[makeQuery(id+"F14.imprint","IMPRINT",EDGE,{"derivedFrom":sQuery(id+"F14.wireOp",EDGE,"E192")}),-1.0]])]});
            extrude(context, id + "F15", {"entities" : qUnion([Q0]), "depth" : 36 * mm});
        }
        {
            var Q0;
            Q0 = qSketchRegion(id + "F13", true);
            extrude(context, id + "F16", {"entities" : qUnion([Q0]), "depth" : 300 * mm});
        }
    });
